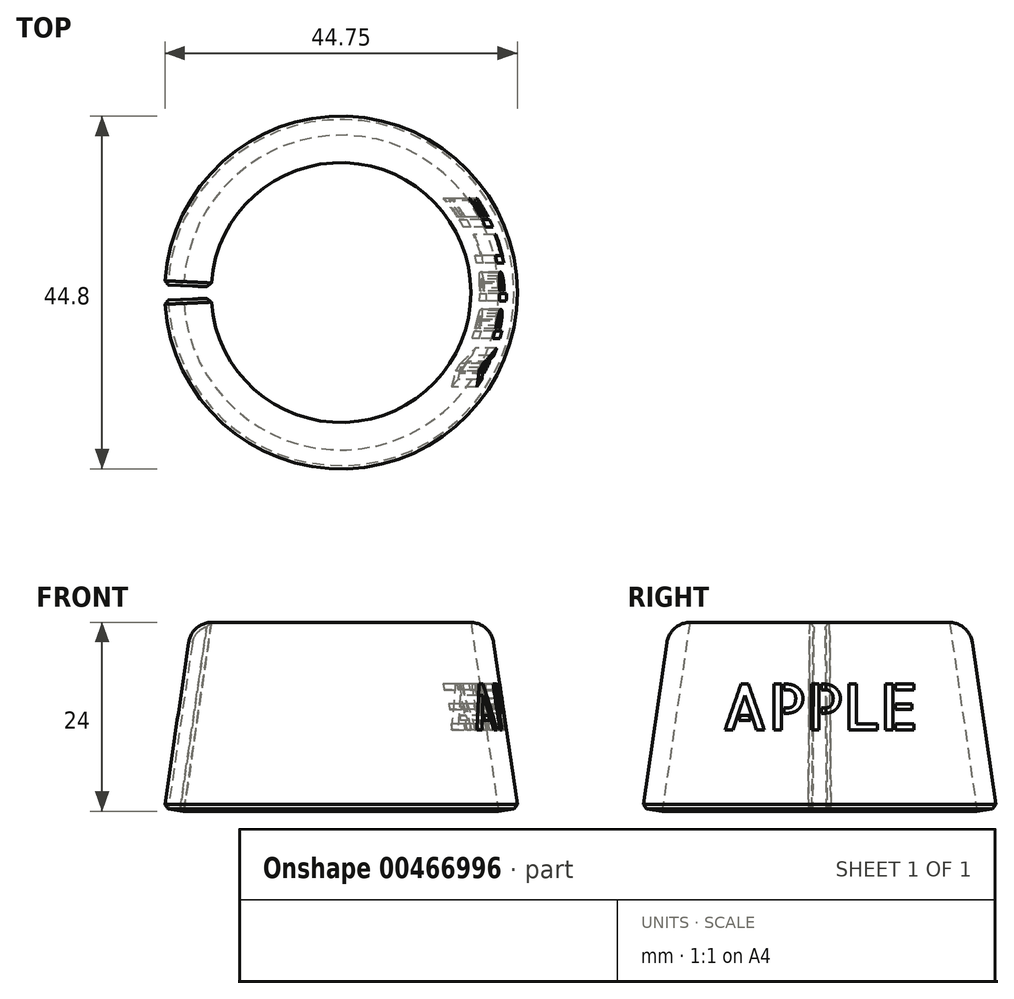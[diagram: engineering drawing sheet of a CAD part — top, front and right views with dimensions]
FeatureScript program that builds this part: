
annotation { "Feature Type Name" : "Feature", "Feature Type Description" : "" }
export const myFeature = defineFeature(function(context is Context, id is Id, definition is map)
    precondition{}
    {
        {
            var Q0;
            Q0=qCreatedBy(makeId("Front.planeOp"),FACE);
            var sketch = newSketch(context, id + "F0", { "sketchPlane" : qUnion([Q0])});
            skLineSegment(sketch, "E0.bottom", {"start": v(0, 0) * mm, "end": v(0, 0) * mm});
            skLineSegment(sketch, "E0.top", {"start": v(0, 24) * mm, "end": v(0, 24) * mm});
            skLineSegment(sketch, "E0.left", {"start": v(0, 0) * mm, "end": v(0, 24) * mm});
            skLineSegment(sketch, "E0.right", {"start": v(0, 0) * mm, "end": v(0, 24) * mm});
            skLineSegment(sketch, "E1.MirrorCS", {"start": v(18.97, 24.36) * mm, "end": v(16.5, 24) * mm});
            skLineSegment(sketch, "E2.MirrorCS", {"start": v(16.5, 24) * mm, "end": v(20, 0) * mm});
            skLineSegment(sketch, "E3.MirrorCS", {"start": v(22.47, 0.36) * mm, "end": v(20, 0) * mm});
            skLineSegment(sketch, "E4.MirrorCS", {"start": v(18.97, 24.36) * mm, "end": v(22.47, 0.36) * mm});
            skSolve(sketch);
        }
        {
            var Q0;
            Q0 = qSketchRegion(id + "F0", true);
            var Q1;
            Q1=sQuery(id+"F0.wireOp",EDGE,"E0.right");
            revolve(context, id + "F1", {"entities" : qUnion([Q0]), "axis" : qUnion([Q1]), "revolveType" : RevolveType.SYMMETRIC, "angle" : 355 * degree});
        }
        {
            var Q0;
            Q0=qCreatedBy(makeId("Right.planeOp"),FACE);
            var sketch = newSketch(context, id + "F2", { "sketchPlane" : qUnion([Q0])});
            skText(sketch, "E5", { "text": "APPLE", "fontName": "AllertaStencil-Regular.ttf"});
            const initialGuessF2  = {"E5": [-0.0125, 0.01036, 1, 0, 0.0058]};
            skSetInitialGuess(sketch, initialGuessF2);
            skSolve(sketch);
        }
        {
            var Q0;
            Q0 = qSketchRegion(id + "F2", true);
            extrude(context, id + "F3", {"entities" : qUnion([Q0]), "operationType" : NewBodyOperationType.REMOVE, "oppositeDirection" : true, "depth" : -50 * mm});
        }
        {
            var Q0;
            Q0=makeQuery(id+"F1.opRevolve","SWEPT_EDGE",EDGE,{"disambiguationData":[OSD([sQuery(id+"F0.wireOp",EDGE,"E1.MirrorCS"),sQuery(id+"F0.wireOp",EDGE,"E4.MirrorCS")])]});
            fillet(context, id + "F4", {"entities" : qUnion([Q0]), "radius" : 3 * mm, "tangentPropagation" : true, "allowEdgeOverflow" : false});
        }
        {
            var Q0;
            Q0=makeQuery(id+"F1.opRevolve","SWEPT_EDGE",EDGE,{"disambiguationData":[OSD([sQuery(id+"F0.wireOp",EDGE,"E3.MirrorCS"),sQuery(id+"F0.wireOp",EDGE,"E4.MirrorCS")])]});
            var Q1;
            Q1=makeQuery(id+"F1.opRevolve","CAP_EDGE",EDGE,{"disambiguationData":[OSD([sQuery(id+"F0.wireOp",EDGE,"E4.MirrorCS")])],"isStart":false});
            var Q2;
            Q2=makeQuery(id+"F1.opRevolve","CAP_EDGE",EDGE,{"disambiguationData":[OSD([sQuery(id+"F0.wireOp",EDGE,"E4.MirrorCS")])],"isStart":true});
            var Q3;
            Q3=makeQuery(id+"F1.opRevolve","CAP_EDGE",EDGE,{"disambiguationData":[OSD([sQuery(id+"F0.wireOp",EDGE,"E2.MirrorCS")])],"isStart":false});
            var Q4;
            Q4=makeQuery(id+"F1.opRevolve","CAP_EDGE",EDGE,{"disambiguationData":[OSD([sQuery(id+"F0.wireOp",EDGE,"E2.MirrorCS")])],"isStart":true});
            chamfer(context, id + "F5", {"entities" : qUnion([Q0, Q1, Q2, Q3, Q4]), "width" : 0.5 * mm, "tangentPropagation" : true});
        }
    });
